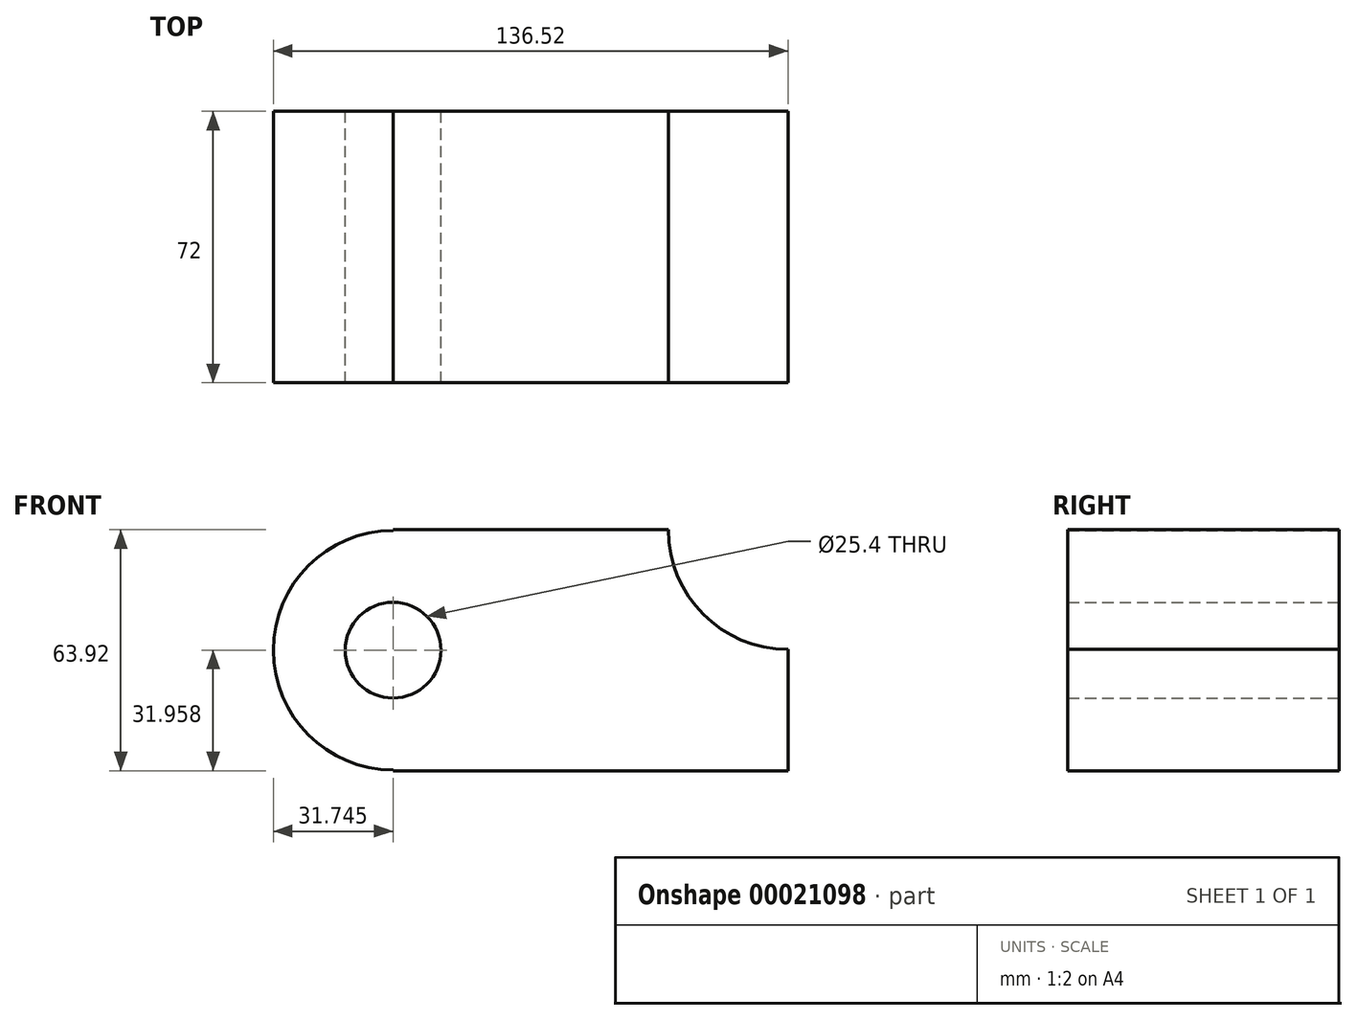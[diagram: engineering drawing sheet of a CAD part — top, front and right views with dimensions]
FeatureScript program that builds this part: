
annotation { "Feature Type Name" : "Feature", "Feature Type Description" : "" }
export const myFeature = defineFeature(function(context is Context, id is Id, definition is map)
    precondition{}
    {
        {
            var Q0;
            Q0=qCreatedBy(makeId("Front.planeOp"),FACE);
            var sketch = newSketch(context, id + "F0", { "sketchPlane" : qUnion([Q0])});
            skLineSegment(sketch, "E0.bottom", {"start": v(-27.41, 34.72) * mm, "end": v(45.61, 34.72) * mm});
            skLineSegment(sketch, "E0.top", {"start": v(-27.41, -29.2) * mm, "end": v(77.36, -29.2) * mm});
            skLineSegment(sketch, "E0.left", {"start": v(-27.41, 34.72) * mm, "end": v(-27.41, -29.2) * mm});
            skLineSegment(sketch, "E0.right", {"start": v(77.36, 2.97) * mm, "end": v(77.36, -29.2) * mm});
            skCircle(sketch, "E1", {"center": v(-27.41, 2.76) * mm, "radius": 31.75 * mm});
            skCircle(sketch, "E2", {"center": v(-27.41, 2.76) * mm, "radius": 12.7 * mm});
            skArc(sketch, "E3", {"start": v(45.61, 34.72) * mm, "mid": v(54.9, 12.27) * mm, "end": v(77.36, 2.97) * mm});
            skSolve(sketch);
        }
        {
            var Q0;
            {var subQ1=sQuery(id+"F0.wireOp",EDGE,"E0.left");var subQ4=sQuery(id+"F0.wireOp",EDGE,"E1");var subQ6=makeQuery(id+"F0.imprint","INTERSECT",VERTEX,{"disambiguationData":[OD(0.0)],"derivedFrom":[subQ1,subQ4]});Q0=makeQuery(id+"F0.imprint","IMPRINT",FACE,{"disambiguationData":[TD([[makeQuery(id+"F0.imprint","IMPRINT",EDGE,{"disambiguationData":[TD([[subQ6,-1.0]])],"derivedFrom":subQ1}),-1.0]])]});}
            var Q1;
            {var subQ1=sQuery(id+"F0.wireOp",EDGE,"E0.left");var subQ4=sQuery(id+"F0.wireOp",EDGE,"E1");var subQ6=makeQuery(id+"F0.imprint","INTERSECT",VERTEX,{"disambiguationData":[OD(0.0)],"derivedFrom":[subQ1,subQ4]});Q1=makeQuery(id+"F0.imprint","IMPRINT",FACE,{"disambiguationData":[TD([[makeQuery(id+"F0.imprint","IMPRINT",EDGE,{"disambiguationData":[TD([[subQ6,-1.0]])],"derivedFrom":subQ1}),1.0]])]});}
            var Q2;
            {var subQ5=sQuery(id+"F0.wireOp",EDGE,"E0.bottom");Q2=makeQuery(id+"F0.imprint","IMPRINT",FACE,{"disambiguationData":[TD([[makeQuery(id+"F0.imprint","IMPRINT",EDGE,{"derivedFrom":subQ5}),-1.0]])]});}
            extrude(context, id + "F1", {"entities" : qUnion([Q0, Q1, Q2]), "depth" : 72 * mm});
        }
    });
